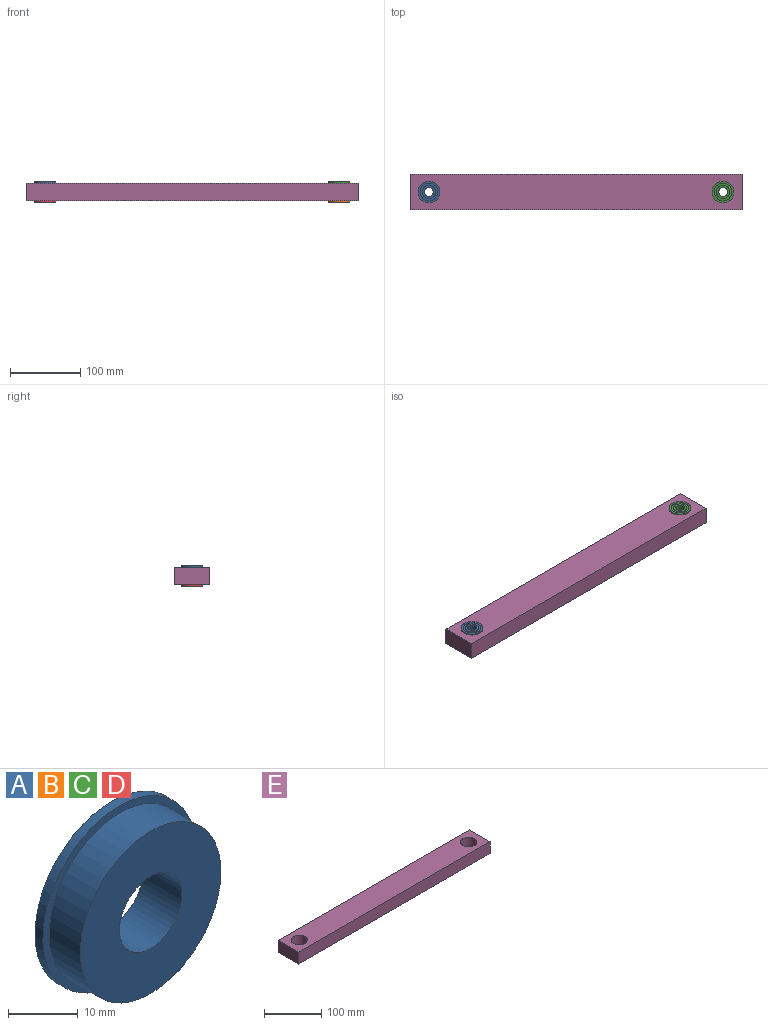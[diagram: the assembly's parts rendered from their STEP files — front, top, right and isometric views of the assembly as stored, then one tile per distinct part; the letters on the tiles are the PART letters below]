
ASSEMBLY  parts=5 mates=4
PART A: 10 faces, bbox 31.1x7.9x31.1 mm
  f0: cylinder r=12.7mm len=25.4mm, axis (0,1,0), area 30.4mm2, adj f8,f9
  f1: cylinder r=15.56mm len=31.12mm, axis (0,1,0), area 155.2mm2, adj f7,f8
  f2: cylinder r=14.29mm len=28.58mm, axis (0,1,0), area 570mm2, adj f6,f7
  f3: cylinder r=6.35mm len=12.7mm, axis (0,1,0), area 316.7mm2, adj f5,f6
  f4: cylinder r=9.53mm len=19.05mm, axis (0,1,0), area 22.8mm2, adj f5,f9
  f5: plane 19.05x19.05mm, normal (0,1,0), area 158.3mm2, adj f3,f4
  f6: plane 28.58x28.58mm, normal (0,-1,0), area 514.6mm2, adj f2,f3
  f7: plane 31.12x31.12mm, normal (0,-1,0), area 119.1mm2, adj f1,f2
  f8: plane 31.12x31.12mm, normal (0,1,0), area 253.7mm2, adj f0,f1
  f9: plane 25.4x25.4mm, normal (0,1,0), area 221.7mm2, adj f0,f4
PART B: same geometry as A
PART C: same geometry as A
PART D: same geometry as A
PART E: 8 faces, bbox 472.2x50.8x25.4 mm
  f0: plane 472.23x25.4mm, normal (0,1,0), area 11994.6mm2, adj f1,f5,f6,f7
  f1: plane 50.8x25.4mm, normal (-1,0,0), area 1290.3mm2, adj f0,f2,f6,f7
  f2: plane 472.23x25.4mm, normal (0,-1,0), area 11994.6mm2, adj f1,f5,f6,f7
  f3: cylinder r=14.29mm len=28.58mm, axis (0,0,-1), area 2280.2mm2, adj f6,f7
  f4: cylinder r=14.29mm len=28.58mm, axis (0,0,-1), area 2280.2mm2, adj f6,f7
  f5: plane 50.8x25.4mm, normal (1,0,0), area 1290.3mm2, adj f0,f2,f6,f7
  f6: plane 472.23x50.8mm, normal (0,0,1), area 22706.6mm2, adj f0,f1,f2,f3,f4,f5
  f7: plane 472.23x50.8mm, normal (0,0,-1), area 22706.6mm2, adj f0,f1,f2,f3,f4,f5
PLACE A rot(axis=(1,0,0),90deg) t=(-218.22,-28.18,-34.64)mm
PLACE B rot(axis=(-1,0,0),90deg) t=(200.03,-28.18,-47.34)mm
PLACE C rot(axis=(1,0,0),90deg) t=(200.03,-28.18,-34.64)mm
PLACE D rot(axis=(-1,0,0),90deg) t=(-218.22,-28.18,-47.34)mm
PLACE E t=(-163.67,-18.09,-53.69)mm
MATE revolute C.f0 <-> E.f4  axis (0,0,-1) through (200.03,-28.18,-28.29)mm
MATE fastened B.f0 <-> E.f4  axis (0,0,1) through (200.03,-28.18,-53.69)mm
MATE revolute A.f0 <-> E.f3  axis (0,0,-1) through (-218.22,-28.18,-28.29)mm
MATE fastened D.f0 <-> E.f3  axis (0,0,1) through (-218.22,-28.18,-53.69)mm
